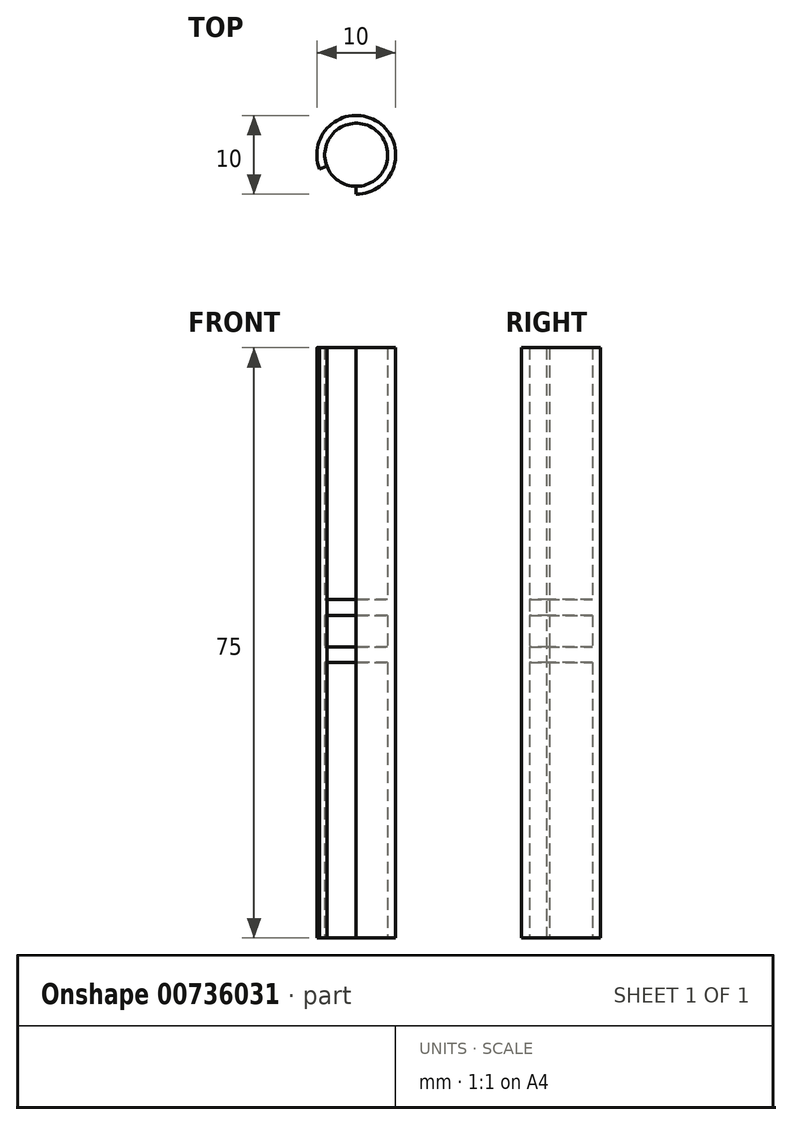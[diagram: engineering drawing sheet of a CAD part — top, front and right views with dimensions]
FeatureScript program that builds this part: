
annotation { "Feature Type Name" : "Feature", "Feature Type Description" : "" }
export const myFeature = defineFeature(function(context is Context, id is Id, definition is map)
    precondition{}
    {
        {
            var Q0;
            Q0=qCreatedBy(makeId("Top.planeOp"),FACE);
            var sketch = newSketch(context, id + "F0", { "sketchPlane" : qUnion([Q0])});
            skCircle(sketch, "E0", {"center": v(0, 0) * mm, "radius": 4 * mm});
            skCircle(sketch, "E1", {"center": v(0, 0) * mm, "radius": 5 * mm});
            skLineSegment(sketch, "E2", {"start": v(0, -4) * mm, "end": v(0, -5) * mm});
            skLineSegment(sketch, "E3", {"start": v(-4.66, -1.81) * mm, "end": v(-3.73, -1.44) * mm});
            skSolve(sketch);
        }
        {
            var Q0;
            {var subQ0=sQuery(id+"F0.wireOp",EDGE,"E2");Q0=makeQuery(id+"F0.imprint","IMPRINT",FACE,{"disambiguationData":[TD([[makeQuery(id+"F0.imprint","IMPRINT",EDGE,{"derivedFrom":subQ0}),1.0]])]});}
            extrude(context, id + "F1", {"entities" : qUnion([Q0]), "depth" : 50 * mm, "offsetDistance" : 25.4 * mm});
        }
        {
            var Q0;
            {var subQ0=sQuery(id+"F0.wireOp",EDGE,"E0");var subQ1=makeQuery(id+"F0.imprint","INTERSECT",VERTEX,{"derivedFrom":[subQ0,sQuery(id+"F0.wireOp",EDGE,"E2")]});Q0=makeQuery(id+"F0.imprint","IMPRINT",FACE,{"disambiguationData":[TD([[makeQuery(id+"F0.imprint","IMPRINT",EDGE,{"disambiguationData":[TD([[subQ1,1.0]])],"derivedFrom":subQ0}),1.0]])]});}
            extrude(context, id + "F2", {"entities" : qUnion([Q0]), "operationType" : NewBodyOperationType.ADD, "depth" : 18 * mm, "offsetDistance" : 25.4 * mm, "hasSecondDirection" : true, "secondDirectionOppositeDirection" : false, "secondDirectionDepth" : 16 * mm});
        }
        {
            var Q0;
            {var subQ0=sQuery(id+"F0.wireOp",EDGE,"E0");var subQ1=makeQuery(id+"F0.imprint","INTERSECT",VERTEX,{"derivedFrom":[subQ0,sQuery(id+"F0.wireOp",EDGE,"E2")]});Q0=makeQuery(id+"F0.imprint","IMPRINT",FACE,{"disambiguationData":[TD([[makeQuery(id+"F0.imprint","IMPRINT",EDGE,{"disambiguationData":[TD([[subQ1,1.0]])],"derivedFrom":subQ0}),1.0]])]});}
            extrude(context, id + "F3", {"entities" : qUnion([Q0]), "operationType" : NewBodyOperationType.ADD, "depth" : 12 * mm, "offsetDistance" : 25.4 * mm, "hasSecondDirection" : true, "secondDirectionOppositeDirection" : false, "secondDirectionDepth" : 10 * mm});
        }
        {
            var Q0;
            {var subQ0=sQuery(id+"F0.wireOp",EDGE,"E2");Q0=makeQuery(id+"F0.imprint","IMPRINT",FACE,{"disambiguationData":[TD([[makeQuery(id+"F0.imprint","IMPRINT",EDGE,{"derivedFrom":subQ0}),1.0]])]});}
            extrude(context, id + "F4", {"entities" : qUnion([Q0]), "operationType" : NewBodyOperationType.ADD, "oppositeDirection" : true, "depth" : 25 * mm, "offsetDistance" : 25.4 * mm});
        }
    });
